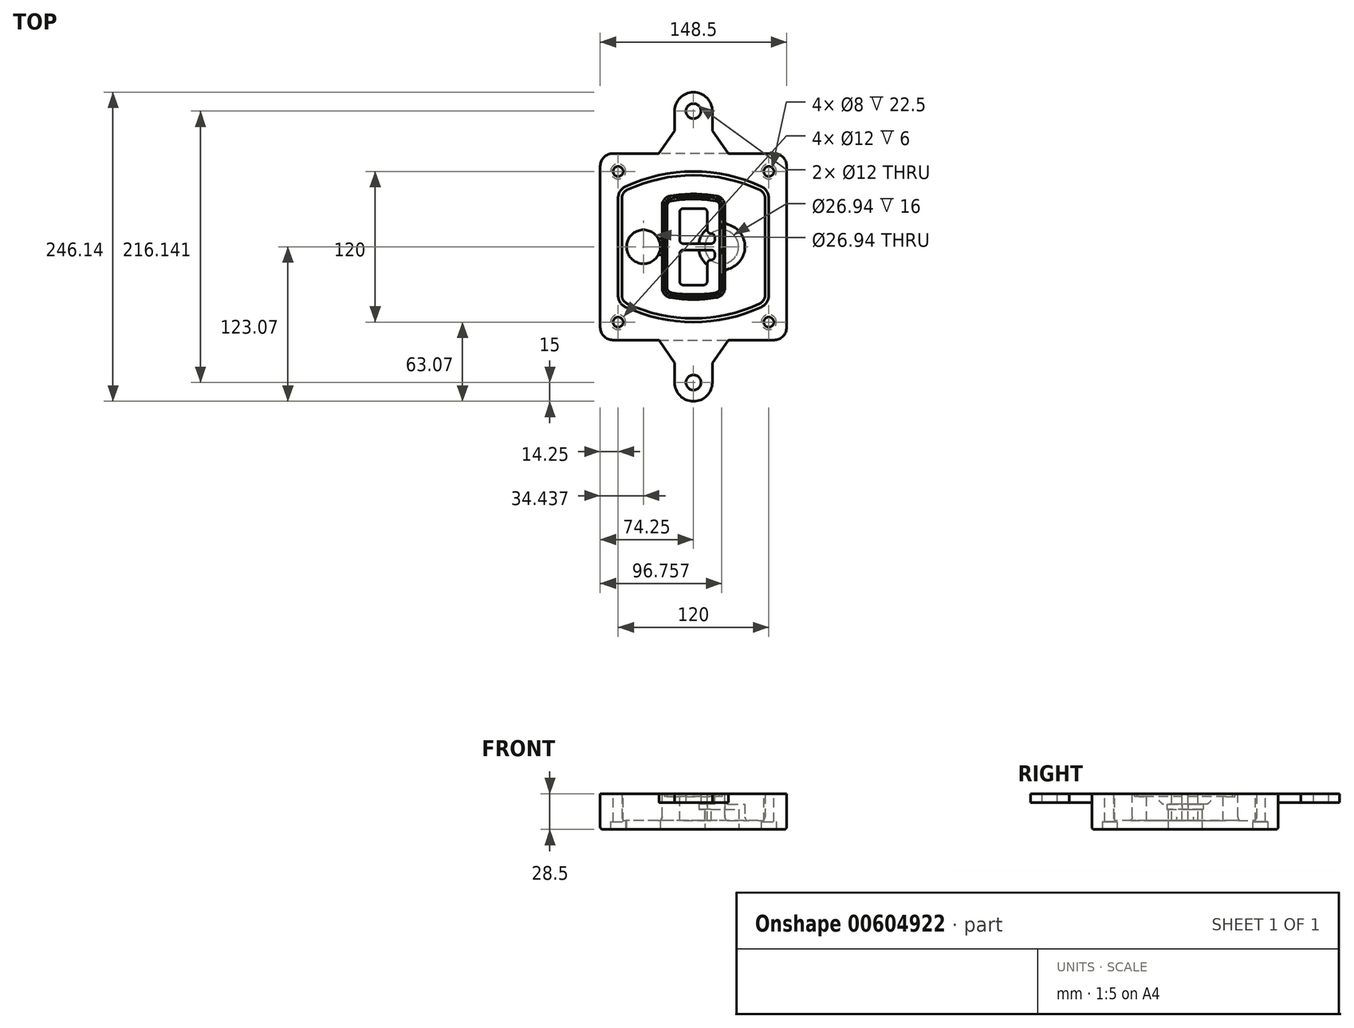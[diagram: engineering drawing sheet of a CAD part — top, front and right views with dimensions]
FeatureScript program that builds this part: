
annotation { "Feature Type Name" : "Feature", "Feature Type Description" : "" }
export const myFeature = defineFeature(function(context is Context, id is Id, definition is map)
    precondition{}
    {
        {
            var Q0;
            Q0=qCreatedBy(makeId("Top.planeOp"),FACE);
            var sketch = newSketch(context, id + "F0", { "sketchPlane" : qUnion([Q0])});
            skPoint(sketch, "E0.rect.middle", {"position": v(0, 0) * mm});
            skLineSegment(sketch, "E1.bottom", {"start": v(-64.25, -74.25) * mm, "end": v(64.25, -74.25) * mm});
            skLineSegment(sketch, "E1.top", {"start": v(-64.25, 74.25) * mm, "end": v(64.25, 74.25) * mm});
            skLineSegment(sketch, "E1.left", {"start": v(-74.25, -64.25) * mm, "end": v(-74.25, 64.25) * mm});
            skLineSegment(sketch, "E1.right", {"start": v(74.25, -64.25) * mm, "end": v(74.25, 64.25) * mm});
            skLineSegment(sketch, "E2", {"start": v(-74.25, 74.25) * mm, "end": v(74.25, -74.25) * mm, "construction": true});
            skLineSegment(sketch, "E3", {"start": v(74.25, 74.25) * mm, "end": v(-74.25, -74.25) * mm, "construction": true});
            skCircle(sketch, "E4", {"center": v(-60, 60) * mm, "radius": 4 * mm});
            skCircle(sketch, "E5", {"center": v(60, 60) * mm, "radius": 4 * mm});
            skCircle(sketch, "E6", {"center": v(60, -60) * mm, "radius": 4 * mm});
            skCircle(sketch, "E7", {"center": v(-60, -60) * mm, "radius": 4 * mm});
            skLineSegment(sketch, "E8", {"start": v(-60, 60) * mm, "end": v(60, 60) * mm, "construction": true});
            skLineSegment(sketch, "E9", {"start": v(60, 60) * mm, "end": v(60, -60) * mm, "construction": true});
            skLineSegment(sketch, "E10", {"start": v(60, -60) * mm, "end": v(-60, -60) * mm, "construction": true});
            skLineSegment(sketch, "E11", {"start": v(-60, -60) * mm, "end": v(-60, 60) * mm, "construction": true});
            skLineSegment(sketch, "E12", {"start": v(-60, 38.83) * mm, "end": v(-60, -38.83) * mm});
            skLineSegment(sketch, "E13", {"start": v(60, 38.83) * mm, "end": v(60, -38.83) * mm});
            skArc(sketch, "E14", {"start": v(54.26, 47.88) * mm, "mid": v(0, 60) * mm, "end": v(-54.26, 47.88) * mm});
            skArc(sketch, "E15", {"start": v(-54.26, -47.88) * mm, "mid": v(0, -60) * mm, "end": v(54.26, -47.88) * mm});
            skLineSegment(sketch, "E16", {"start": v(-60, 0) * mm, "end": v(60, 0) * mm, "construction": true});
            skPoint(sketch, "E17.visualSharp", {"position": v(-60, -45) * mm});
            skArc(sketch, "E17.filletArc", {"start": v(-60, -38.83) * mm, "mid": v(-58.44, -44.2) * mm, "end": v(-54.26, -47.88) * mm});
            skPoint(sketch, "E18.visualSharp", {"position": v(-60, 45) * mm});
            skArc(sketch, "E18.filletArc", {"start": v(-54.26, 47.88) * mm, "mid": v(-58.44, 44.2) * mm, "end": v(-60, 38.83) * mm});
            skPoint(sketch, "E19.visualSharp", {"position": v(60, 45) * mm});
            skArc(sketch, "E19.filletArc", {"start": v(60, 38.83) * mm, "mid": v(58.44, 44.2) * mm, "end": v(54.26, 47.88) * mm});
            skPoint(sketch, "E20.visualSharp", {"position": v(60, -45) * mm});
            skArc(sketch, "E20.filletArc", {"start": v(54.26, -47.88) * mm, "mid": v(58.44, -44.2) * mm, "end": v(60, -38.83) * mm});
            skPoint(sketch, "E21.visualSharp", {"position": v(-74.25, 74.25) * mm});
            skArc(sketch, "E21.filletArc", {"start": v(-64.25, 74.25) * mm, "mid": v(-71.32, 71.32) * mm, "end": v(-74.25, 64.25) * mm});
            skPoint(sketch, "E22.visualSharp", {"position": v(74.25, 74.25) * mm});
            skArc(sketch, "E22.filletArc", {"start": v(74.25, 64.25) * mm, "mid": v(71.32, 71.32) * mm, "end": v(64.25, 74.25) * mm});
            skPoint(sketch, "E23.visualSharp", {"position": v(74.25, -74.25) * mm});
            skArc(sketch, "E23.filletArc", {"start": v(64.25, -74.25) * mm, "mid": v(71.32, -71.32) * mm, "end": v(74.25, -64.25) * mm});
            skPoint(sketch, "E24.visualSharp", {"position": v(-74.25, -74.25) * mm});
            skArc(sketch, "E24.filletArc", {"start": v(-74.25, -64.25) * mm, "mid": v(-71.32, -71.32) * mm, "end": v(-64.25, -74.25) * mm});
            skArc(sketch, "E25.0", {"start": v(57, 38.83) * mm, "mid": v(55.9, 42.58) * mm, "end": v(52.98, 45.17) * mm});
            skLineSegment(sketch, "E25.1", {"start": v(57, 38.83) * mm, "end": v(57, -38.83) * mm});
            skArc(sketch, "E25.2", {"start": v(52.98, -45.17) * mm, "mid": v(55.9, -42.58) * mm, "end": v(57, -38.83) * mm});
            skArc(sketch, "E25.3", {"start": v(-52.98, -45.17) * mm, "mid": v(0, -57) * mm, "end": v(52.98, -45.17) * mm});
            skArc(sketch, "E25.4", {"start": v(-57, -38.83) * mm, "mid": v(-55.9, -42.58) * mm, "end": v(-52.98, -45.17) * mm});
            skArc(sketch, "E25.5", {"start": v(52.98, 45.17) * mm, "mid": v(0, 57) * mm, "end": v(-52.98, 45.17) * mm});
            skLineSegment(sketch, "E25.6", {"start": v(-57, 38.83) * mm, "end": v(-57, -38.83) * mm});
            skArc(sketch, "E25.7", {"start": v(-52.98, 45.17) * mm, "mid": v(-55.9, 42.58) * mm, "end": v(-57, 38.83) * mm});
            skArc(sketch, "E26.0", {"start": v(-55.96, 51.5) * mm, "mid": v(-61.82, 46.33) * mm, "end": v(-64, 38.83) * mm});
            skArc(sketch, "E26.1", {"start": v(55.96, 51.5) * mm, "mid": v(0, 64) * mm, "end": v(-55.96, 51.5) * mm});
            skArc(sketch, "E26.2", {"start": v(64, 38.83) * mm, "mid": v(61.82, 46.33) * mm, "end": v(55.96, 51.5) * mm});
            skLineSegment(sketch, "E26.3", {"start": v(64, 38.83) * mm, "end": v(64, -38.83) * mm});
            skArc(sketch, "E26.4", {"start": v(55.96, -51.5) * mm, "mid": v(61.82, -46.33) * mm, "end": v(64, -38.83) * mm});
            skLineSegment(sketch, "E26.5", {"start": v(-64, 38.83) * mm, "end": v(-64, -38.83) * mm});
            skArc(sketch, "E26.6", {"start": v(-55.96, -51.5) * mm, "mid": v(0, -64) * mm, "end": v(55.96, -51.5) * mm});
            skArc(sketch, "E26.7", {"start": v(-64, -38.83) * mm, "mid": v(-61.82, -46.33) * mm, "end": v(-55.96, -51.5) * mm});
            skSolve(sketch);
        }
        {
            var Q0;
            Q0=makeQuery(id+"F0.imprint","IMPRINT",FACE,{"disambiguationData":[TD([[makeQuery(id+"F0.imprint","IMPRINT",EDGE,{"derivedFrom":sQuery(id+"F0.wireOp",EDGE,"E1.bottom")}),1.0]])]});
            var Q1;
            Q1=makeQuery(id+"F0.imprint","IMPRINT",FACE,{"disambiguationData":[TD([[makeQuery(id+"F0.imprint","IMPRINT",EDGE,{"derivedFrom":sQuery(id+"F0.wireOp",EDGE,"E12")}),1.0]])]});
            var Q2;
            Q2=makeQuery(id+"F0.imprint","IMPRINT",FACE,{"disambiguationData":[TD([[makeQuery(id+"F0.imprint","IMPRINT",EDGE,{"derivedFrom":sQuery(id+"F0.wireOp",EDGE,"E25.0")}),1.0]])]});
            var Q3;
            Q3=makeQuery(id+"F0.imprint","IMPRINT",FACE,{"disambiguationData":[TD([[makeQuery(id+"F0.imprint","IMPRINT",EDGE,{"derivedFrom":sQuery(id+"F0.wireOp",EDGE,"E12")}),-1.0]])]});
            extrude(context, id + "F1", {"entities" : qUnion([Q0, Q1, Q2, Q3]), "oppositeDirection" : true, "depth" : 25 * mm});
        }
        {
            var Q0;
            Q0=makeQuery(id+"F0.imprint","IMPRINT",FACE,{"disambiguationData":[TD([[makeQuery(id+"F0.imprint","IMPRINT",EDGE,{"derivedFrom":sQuery(id+"F0.wireOp",EDGE,"E12")}),1.0]])]});
            extrude(context, id + "F2", {"entities" : qUnion([Q0]), "operationType" : NewBodyOperationType.ADD, "depth" : 3 * mm});
        }
        {
            var Q0;
            Q0=makeQuery(id+"F0.imprint","IMPRINT",FACE,{"disambiguationData":[TD([[makeQuery(id+"F0.imprint","IMPRINT",EDGE,{"derivedFrom":sQuery(id+"F0.wireOp",EDGE,"E25.0")}),1.0]])]});
            extrude(context, id + "F3", {"entities" : qUnion([Q0]), "operationType" : NewBodyOperationType.REMOVE, "oppositeDirection" : true, "depth" : 18 * mm});
        }
        {
            var Q0;
            Q0=makeQuery(id+"F2.opExtrude","CAP_FACE",FACE,{"disambiguationData":[OSD([sQuery(id+"F0.wireOp",EDGE,"E12"),sQuery(id+"F0.wireOp",EDGE,"E13"),sQuery(id+"F0.wireOp",EDGE,"E14"),sQuery(id+"F0.wireOp",EDGE,"E15"),sQuery(id+"F0.wireOp",EDGE,"E17.filletArc"),sQuery(id+"F0.wireOp",EDGE,"E18.filletArc"),sQuery(id+"F0.wireOp",EDGE,"E19.filletArc"),sQuery(id+"F0.wireOp",EDGE,"E20.filletArc"),sQuery(id+"F0.wireOp",EDGE,"E25.0"),sQuery(id+"F0.wireOp",EDGE,"E25.1"),sQuery(id+"F0.wireOp",EDGE,"E25.2"),sQuery(id+"F0.wireOp",EDGE,"E25.3"),sQuery(id+"F0.wireOp",EDGE,"E25.4"),sQuery(id+"F0.wireOp",EDGE,"E25.5"),sQuery(id+"F0.wireOp",EDGE,"E25.6"),sQuery(id+"F0.wireOp",EDGE,"E25.7")])],"isStart":false});
            var sketch = newSketch(context, id + "F4", { "sketchPlane" : qUnion([Q0])});
            skArc(sketch, "E27.0", {"start": v(-18.34, -40.45) * mm, "mid": v(0, -42) * mm, "end": v(18.34, -40.45) * mm});
            skArc(sketch, "E28.0", {"start": v(18.34, 40.45) * mm, "mid": v(0, 42) * mm, "end": v(-18.34, 40.45) * mm});
            skLineSegment(sketch, "E29", {"start": v(-25, 32.57) * mm, "end": v(-25, -32.57) * mm});
            skLineSegment(sketch, "E30", {"start": v(25, 32.57) * mm, "end": v(25, -32.57) * mm});
            skLineSegment(sketch, "E31", {"start": v(-25, 39.1) * mm, "end": v(25, 39.1) * mm, "construction": true});
            skLineSegment(sketch, "E32", {"start": v(-25, -39.1) * mm, "end": v(25, -39.1) * mm, "construction": true});
            skPoint(sketch, "E33.visualSharp", {"position": v(-25, 39.1) * mm});
            skArc(sketch, "E33.filletArc", {"start": v(-18.34, 40.45) * mm, "mid": v(-23.11, 37.73) * mm, "end": v(-25, 32.57) * mm});
            skPoint(sketch, "E34.visualSharp", {"position": v(25, 39.1) * mm});
            skArc(sketch, "E34.filletArc", {"start": v(25, 32.57) * mm, "mid": v(23.11, 37.73) * mm, "end": v(18.34, 40.45) * mm});
            skPoint(sketch, "E35.visualSharp", {"position": v(25, -39.1) * mm});
            skArc(sketch, "E35.filletArc", {"start": v(18.34, -40.45) * mm, "mid": v(23.11, -37.73) * mm, "end": v(25, -32.57) * mm});
            skPoint(sketch, "E36.visualSharp", {"position": v(-25, -39.1) * mm});
            skArc(sketch, "E36.filletArc", {"start": v(-25, -32.57) * mm, "mid": v(-23.11, -37.73) * mm, "end": v(-18.34, -40.45) * mm});
            skArc(sketch, "E37.0", {"start": v(52.98, 45.17) * mm, "mid": v(0, 57) * mm, "end": v(-52.98, 45.17) * mm});
            skArc(sketch, "E37.1", {"start": v(-52.98, 45.17) * mm, "mid": v(-55.9, 42.58) * mm, "end": v(-57, 38.83) * mm});
            skLineSegment(sketch, "E37.2", {"start": v(-57, 38.83) * mm, "end": v(-57, -38.83) * mm});
            skArc(sketch, "E37.3", {"start": v(-57, -38.83) * mm, "mid": v(-55.9, -42.58) * mm, "end": v(-52.98, -45.17) * mm});
            skArc(sketch, "E37.4", {"start": v(-52.98, -45.17) * mm, "mid": v(0, -57) * mm, "end": v(52.98, -45.17) * mm});
            skArc(sketch, "E37.5", {"start": v(52.98, -45.17) * mm, "mid": v(55.9, -42.58) * mm, "end": v(57, -38.83) * mm});
            skLineSegment(sketch, "E37.6", {"start": v(57, 38.83) * mm, "end": v(57, -38.83) * mm});
            skArc(sketch, "E37.7", {"start": v(57, 38.83) * mm, "mid": v(55.9, 42.58) * mm, "end": v(52.98, 45.17) * mm});
            skLineSegment(sketch, "E38.0", {"start": v(23, 32.57) * mm, "end": v(23, -32.57) * mm});
            skArc(sketch, "E38.1", {"start": v(18, -38.48) * mm, "mid": v(21.58, -36.44) * mm, "end": v(23, -32.57) * mm});
            skArc(sketch, "E38.2", {"start": v(-18, -38.48) * mm, "mid": v(0, -40) * mm, "end": v(18, -38.48) * mm});
            skArc(sketch, "E38.3", {"start": v(-23, -32.57) * mm, "mid": v(-21.58, -36.44) * mm, "end": v(-18, -38.48) * mm});
            skLineSegment(sketch, "E38.4", {"start": v(-23, 32.57) * mm, "end": v(-23, -32.57) * mm});
            skArc(sketch, "E38.5", {"start": v(23, 32.57) * mm, "mid": v(21.58, 36.44) * mm, "end": v(18, 38.48) * mm});
            skArc(sketch, "E38.6", {"start": v(-18, 38.48) * mm, "mid": v(-21.58, 36.44) * mm, "end": v(-23, 32.57) * mm});
            skArc(sketch, "E38.7", {"start": v(18, 38.48) * mm, "mid": v(0, 40) * mm, "end": v(-18, 38.48) * mm});
            skArc(sketch, "E39.0", {"start": v(21, 32.57) * mm, "mid": v(20.06, 35.15) * mm, "end": v(17.67, 36.5) * mm});
            skLineSegment(sketch, "E39.1", {"start": v(21, 32.57) * mm, "end": v(21, -32.57) * mm});
            skArc(sketch, "E39.2", {"start": v(17.67, -36.5) * mm, "mid": v(20.06, -35.15) * mm, "end": v(21, -32.57) * mm});
            skArc(sketch, "E39.3", {"start": v(-17.67, -36.5) * mm, "mid": v(0, -38) * mm, "end": v(17.67, -36.5) * mm});
            skArc(sketch, "E39.4", {"start": v(-21, -32.57) * mm, "mid": v(-20.06, -35.15) * mm, "end": v(-17.67, -36.5) * mm});
            skArc(sketch, "E39.5", {"start": v(17.67, 36.5) * mm, "mid": v(0, 38) * mm, "end": v(-17.67, 36.5) * mm});
            skLineSegment(sketch, "E39.6", {"start": v(-21, 32.57) * mm, "end": v(-21, -32.57) * mm});
            skArc(sketch, "E39.7", {"start": v(-17.67, 36.5) * mm, "mid": v(-20.06, 35.15) * mm, "end": v(-21, 32.57) * mm});
            skLineSegment(sketch, "E40", {"start": v(-25, 0) * mm, "end": v(25, 0) * mm, "construction": true});
            skLineSegment(sketch, "E41", {"start": v(-11, 5.5) * mm, "end": v(-11, 27.5) * mm});
            skLineSegment(sketch, "E42", {"start": v(-8, 30.5) * mm, "end": v(8, 30.5) * mm});
            skLineSegment(sketch, "E43", {"start": v(11, 27.5) * mm, "end": v(11, 13.5) * mm});
            skLineSegment(sketch, "E44", {"start": v(14, 10.5) * mm, "end": v(14, 10.5) * mm});
            skLineSegment(sketch, "E45", {"start": v(17, 7.5) * mm, "end": v(17, 5.5) * mm});
            skLineSegment(sketch, "E46", {"start": v(14, 2.5) * mm, "end": v(-8, 2.5) * mm});
            skPoint(sketch, "E47.visualSharp", {"position": v(-11, 30.5) * mm});
            skArc(sketch, "E47.filletArc", {"start": v(-8, 30.5) * mm, "mid": v(-10.12, 29.62) * mm, "end": v(-11, 27.5) * mm});
            skPoint(sketch, "E48.visualSharp", {"position": v(11, 30.5) * mm});
            skArc(sketch, "E48.filletArc", {"start": v(11, 27.5) * mm, "mid": v(10.12, 29.62) * mm, "end": v(8, 30.5) * mm});
            skPoint(sketch, "E49.visualSharp", {"position": v(11, 10.5) * mm});
            skArc(sketch, "E49.filletArc", {"start": v(11, 13.5) * mm, "mid": v(11.88, 11.38) * mm, "end": v(14, 10.5) * mm});
            skPoint(sketch, "E50.visualSharp", {"position": v(17, 10.5) * mm});
            skArc(sketch, "E50.filletArc", {"start": v(17, 7.5) * mm, "mid": v(16.12, 9.62) * mm, "end": v(14, 10.5) * mm});
            skPoint(sketch, "E51.visualSharp", {"position": v(17, 2.5) * mm});
            skArc(sketch, "E51.filletArc", {"start": v(14, 2.5) * mm, "mid": v(16.12, 3.38) * mm, "end": v(17, 5.5) * mm});
            skPoint(sketch, "E52.visualSharp", {"position": v(-11, 2.5) * mm});
            skArc(sketch, "E52.filletArc", {"start": v(-11, 5.5) * mm, "mid": v(-10.12, 3.38) * mm, "end": v(-8, 2.5) * mm});
            skLineSegment(sketch, "E53.0.MirrorCS", {"start": v(14, -2.5) * mm, "end": v(-8, -2.5) * mm});
            skArc(sketch, "E54.0.MirrorCS", {"start": v(-11, -5.5) * mm, "mid": v(-10.12, -3.38) * mm, "end": v(-8, -2.5) * mm});
            skLineSegment(sketch, "E55.0.MirrorCS", {"start": v(-11, -5.5) * mm, "end": v(-11, -27.5) * mm});
            skArc(sketch, "E56.0.MirrorCS", {"start": v(-8, -30.5) * mm, "mid": v(-10.12, -29.62) * mm, "end": v(-11, -27.5) * mm});
            skLineSegment(sketch, "E57.0.MirrorCS", {"start": v(-8, -30.5) * mm, "end": v(8, -30.5) * mm});
            skArc(sketch, "E58.0.MirrorCS", {"start": v(11, -27.5) * mm, "mid": v(10.12, -29.62) * mm, "end": v(8, -30.5) * mm});
            skLineSegment(sketch, "E59.0.MirrorCS", {"start": v(11, -27.5) * mm, "end": v(11, -13.5) * mm});
            skArc(sketch, "E60.0.MirrorCS", {"start": v(11, -13.5) * mm, "mid": v(11.88, -11.38) * mm, "end": v(14, -10.5) * mm});
            skArc(sketch, "E61.0.MirrorCS", {"start": v(17, -7.5) * mm, "mid": v(16.12, -9.62) * mm, "end": v(14, -10.5) * mm});
            skLineSegment(sketch, "E62.0.MirrorCS", {"start": v(17, -7.5) * mm, "end": v(17, -5.5) * mm});
            skArc(sketch, "E63.0.MirrorCS", {"start": v(14, -2.5) * mm, "mid": v(16.12, -3.38) * mm, "end": v(17, -5.5) * mm});
            skSolve(sketch);
        }
        {
            var Q0;
            Q0=makeQuery(id+"F4.imprint","IMPRINT",FACE,{"disambiguationData":[TD([[makeQuery(id+"F4.imprint","IMPRINT",EDGE,{"derivedFrom":sQuery(id+"F4.wireOp",EDGE,"E27.0")}),1.0]])]});
            var Q1;
            Q1=makeQuery(id+"F4.imprint","IMPRINT",FACE,{"disambiguationData":[TD([[makeQuery(id+"F4.imprint","IMPRINT",EDGE,{"derivedFrom":sQuery(id+"F4.wireOp",EDGE,"E38.0")}),-1.0]])]});
            var Q2;
            Q2=makeQuery(id+"F4.imprint","IMPRINT",FACE,{"disambiguationData":[TD([[makeQuery(id+"F4.imprint","IMPRINT",EDGE,{"derivedFrom":sQuery(id+"F4.wireOp",EDGE,"E39.0")}),1.0]])]});
            extrude(context, id + "F5", {"entities" : qUnion([Q0, Q1, Q2]), "operationType" : NewBodyOperationType.ADD, "endBound" : BoundingType.UP_TO_NEXT, "oppositeDirection" : true, "depth" : 25 * mm});
        }
        {
            var Q0;
            Q0=makeQuery(id+"F4.imprint","IMPRINT",FACE,{"disambiguationData":[TD([[makeQuery(id+"F4.imprint","IMPRINT",EDGE,{"derivedFrom":sQuery(id+"F4.wireOp",EDGE,"E38.0")}),-1.0]])]});
            extrude(context, id + "F6", {"entities" : qUnion([Q0]), "operationType" : NewBodyOperationType.REMOVE, "oppositeDirection" : true, "depth" : 2 * mm});
        }
        {
            var Q0;
            Q0=makeQuery(id+"F1.opExtrude","CAP_FACE",FACE,{"disambiguationData":[OSD([sQuery(id+"F0.wireOp",EDGE,"E1.bottom"),sQuery(id+"F0.wireOp",EDGE,"E1.top"),sQuery(id+"F0.wireOp",EDGE,"E1.left"),sQuery(id+"F0.wireOp",EDGE,"E1.right"),sQuery(id+"F0.wireOp",EDGE,"E4"),sQuery(id+"F0.wireOp",EDGE,"E5"),sQuery(id+"F0.wireOp",EDGE,"E6"),sQuery(id+"F0.wireOp",EDGE,"E7"),sQuery(id+"F0.wireOp",EDGE,"E21.filletArc"),sQuery(id+"F0.wireOp",EDGE,"E22.filletArc"),sQuery(id+"F0.wireOp",EDGE,"E23.filletArc"),sQuery(id+"F0.wireOp",EDGE,"E24.filletArc")])],"isStart":false});
            var sketch = newSketch(context, id + "F7", { "sketchPlane" : qUnion([Q0])});
            skCircle(sketch, "E64", {"center": v(22.5, 0) * mm, "radius": 13.47 * mm});
            skCircle(sketch, "E65", {"center": v(-39.81, 0) * mm, "radius": 13.47 * mm});
            skLineSegment(sketch, "E66", {"start": v(74.25, 0) * mm, "end": v(-74.25, 0) * mm});
            skCircle(sketch, "E67", {"center": v(22.5, 0) * mm, "radius": 18.47 * mm});
            skCircle(sketch, "E68", {"center": v(60, -60) * mm, "radius": 6 * mm});
            skCircle(sketch, "E69", {"center": v(-60, -60) * mm, "radius": 6 * mm});
            skCircle(sketch, "E70", {"center": v(-60, 60) * mm, "radius": 6 * mm});
            skCircle(sketch, "E71", {"center": v(60, 60) * mm, "radius": 6 * mm});
            skSolve(sketch);
        }
        {
            var Q0;
            {var subQ1=sQuery(id+"F7.wireOp",EDGE,"E66");var subQ4=sQuery(id+"F7.wireOp",EDGE,"E64");var subQ6=makeQuery(id+"F7.imprint","INTERSECT",VERTEX,{"disambiguationData":[OD(0.0)],"derivedFrom":[subQ4,subQ1]});Q0=makeQuery(id+"F7.imprint","IMPRINT",FACE,{"disambiguationData":[TD([[makeQuery(id+"F7.imprint","IMPRINT",EDGE,{"disambiguationData":[TD([[subQ6,-1.0]])],"derivedFrom":subQ4}),-1.0]])]});}
            var Q1;
            {var subQ0=sQuery(id+"F7.wireOp",EDGE,"E66");var subQ1=sQuery(id+"F7.wireOp",EDGE,"E64");var subQ3=makeQuery(id+"F7.imprint","INTERSECT",VERTEX,{"disambiguationData":[OD(0.0)],"derivedFrom":[subQ1,subQ0]});Q1=makeQuery(id+"F7.imprint","IMPRINT",FACE,{"disambiguationData":[TD([[makeQuery(id+"F7.imprint","IMPRINT",EDGE,{"disambiguationData":[TD([[subQ3,-1.0]])],"derivedFrom":subQ1}),1.0]])]});}
            var Q2;
            {var subQ0=sQuery(id+"F7.wireOp",EDGE,"E66");var subQ1=sQuery(id+"F7.wireOp",EDGE,"E64");var subQ3=makeQuery(id+"F7.imprint","INTERSECT",VERTEX,{"disambiguationData":[OD(0.0)],"derivedFrom":[subQ1,subQ0]});Q2=makeQuery(id+"F7.imprint","IMPRINT",FACE,{"disambiguationData":[TD([[makeQuery(id+"F7.imprint","IMPRINT",EDGE,{"disambiguationData":[TD([[subQ3,1.0]])],"derivedFrom":subQ1}),1.0]])]});}
            var Q3;
            {var subQ1=sQuery(id+"F7.wireOp",EDGE,"E66");var subQ4=sQuery(id+"F7.wireOp",EDGE,"E64");var subQ6=makeQuery(id+"F7.imprint","INTERSECT",VERTEX,{"disambiguationData":[OD(0.0)],"derivedFrom":[subQ4,subQ1]});Q3=makeQuery(id+"F7.imprint","IMPRINT",FACE,{"disambiguationData":[TD([[makeQuery(id+"F7.imprint","IMPRINT",EDGE,{"disambiguationData":[TD([[subQ6,1.0]])],"derivedFrom":subQ4}),-1.0]])]});}
            extrude(context, id + "F8", {"entities" : qUnion([Q0, Q1, Q2, Q3]), "operationType" : NewBodyOperationType.ADD, "oppositeDirection" : true, "depth" : 20 * mm});
        }
        {
            var Q0;
            {var subQ0=sQuery(id+"F7.wireOp",EDGE,"E66");var subQ1=sQuery(id+"F7.wireOp",EDGE,"E64");var subQ3=makeQuery(id+"F7.imprint","INTERSECT",VERTEX,{"disambiguationData":[OD(0.0)],"derivedFrom":[subQ1,subQ0]});Q0=makeQuery(id+"F7.imprint","IMPRINT",FACE,{"disambiguationData":[TD([[makeQuery(id+"F7.imprint","IMPRINT",EDGE,{"disambiguationData":[TD([[subQ3,-1.0]])],"derivedFrom":subQ1}),1.0]])]});}
            var Q1;
            {var subQ0=sQuery(id+"F7.wireOp",EDGE,"E66");var subQ1=sQuery(id+"F7.wireOp",EDGE,"E64");var subQ3=makeQuery(id+"F7.imprint","INTERSECT",VERTEX,{"disambiguationData":[OD(0.0)],"derivedFrom":[subQ1,subQ0]});Q1=makeQuery(id+"F7.imprint","IMPRINT",FACE,{"disambiguationData":[TD([[makeQuery(id+"F7.imprint","IMPRINT",EDGE,{"disambiguationData":[TD([[subQ3,1.0]])],"derivedFrom":subQ1}),1.0]])]});}
            extrude(context, id + "F9", {"entities" : qUnion([Q0, Q1]), "operationType" : NewBodyOperationType.REMOVE, "oppositeDirection" : true, "depth" : 16 * mm});
        }
        {
            var Q0;
            {var subQ0=sQuery(id+"F7.wireOp",EDGE,"E66");var subQ1=sQuery(id+"F7.wireOp",EDGE,"E65");var subQ3=makeQuery(id+"F7.imprint","INTERSECT",VERTEX,{"disambiguationData":[OD(0.0)],"derivedFrom":[subQ1,subQ0]});Q0=makeQuery(id+"F7.imprint","IMPRINT",FACE,{"disambiguationData":[TD([[makeQuery(id+"F7.imprint","IMPRINT",EDGE,{"disambiguationData":[TD([[subQ3,-1.0]])],"derivedFrom":subQ1}),1.0]])]});}
            var Q1;
            {var subQ0=sQuery(id+"F7.wireOp",EDGE,"E66");var subQ1=sQuery(id+"F7.wireOp",EDGE,"E65");var subQ3=makeQuery(id+"F7.imprint","INTERSECT",VERTEX,{"disambiguationData":[OD(0.0)],"derivedFrom":[subQ1,subQ0]});Q1=makeQuery(id+"F7.imprint","IMPRINT",FACE,{"disambiguationData":[TD([[makeQuery(id+"F7.imprint","IMPRINT",EDGE,{"disambiguationData":[TD([[subQ3,1.0]])],"derivedFrom":subQ1}),1.0]])]});}
            extrude(context, id + "F10", {"entities" : qUnion([Q0, Q1]), "operationType" : NewBodyOperationType.REMOVE, "oppositeDirection" : true, "depth" : 25 * mm});
        }
        {
            var Q0;
            Q0=makeQuery(id+"F7.imprint","IMPRINT",FACE,{"disambiguationData":[TD([[makeQuery(id+"F7.imprint","IMPRINT",EDGE,{"derivedFrom":sQuery(id+"F7.wireOp",EDGE,"E68")}),1.0]])]});
            var Q1;
            Q1=makeQuery(id+"F7.imprint","IMPRINT",FACE,{"disambiguationData":[TD([[makeQuery(id+"F7.imprint","IMPRINT",EDGE,{"derivedFrom":makeQuery(id+"F1.opExtrude","CAP_EDGE",EDGE,{"disambiguationData":[OSD([sQuery(id+"F0.wireOp",EDGE,"E5")])],"isStart":false})}),-1.0]])]});
            var Q2;
            Q2=makeQuery(id+"F7.imprint","IMPRINT",FACE,{"disambiguationData":[TD([[makeQuery(id+"F7.imprint","IMPRINT",EDGE,{"derivedFrom":sQuery(id+"F7.wireOp",EDGE,"E69")}),1.0]])]});
            var Q3;
            Q3=makeQuery(id+"F7.imprint","IMPRINT",FACE,{"disambiguationData":[TD([[makeQuery(id+"F7.imprint","IMPRINT",EDGE,{"derivedFrom":makeQuery(id+"F1.opExtrude","CAP_EDGE",EDGE,{"disambiguationData":[OSD([sQuery(id+"F0.wireOp",EDGE,"E4")])],"isStart":false})}),-1.0]])]});
            var Q4;
            Q4=makeQuery(id+"F7.imprint","IMPRINT",FACE,{"disambiguationData":[TD([[makeQuery(id+"F7.imprint","IMPRINT",EDGE,{"derivedFrom":sQuery(id+"F7.wireOp",EDGE,"E70")}),1.0]])]});
            var Q5;
            Q5=makeQuery(id+"F7.imprint","IMPRINT",FACE,{"disambiguationData":[TD([[makeQuery(id+"F7.imprint","IMPRINT",EDGE,{"derivedFrom":makeQuery(id+"F1.opExtrude","CAP_EDGE",EDGE,{"disambiguationData":[OSD([sQuery(id+"F0.wireOp",EDGE,"E7")])],"isStart":false})}),-1.0]])]});
            var Q6;
            Q6=makeQuery(id+"F7.imprint","IMPRINT",FACE,{"disambiguationData":[TD([[makeQuery(id+"F7.imprint","IMPRINT",EDGE,{"derivedFrom":sQuery(id+"F7.wireOp",EDGE,"E71")}),1.0]])]});
            var Q7;
            Q7=makeQuery(id+"F7.imprint","IMPRINT",FACE,{"disambiguationData":[TD([[makeQuery(id+"F7.imprint","IMPRINT",EDGE,{"derivedFrom":makeQuery(id+"F1.opExtrude","CAP_EDGE",EDGE,{"disambiguationData":[OSD([sQuery(id+"F0.wireOp",EDGE,"E6")])],"isStart":false})}),-1.0]])]});
            extrude(context, id + "F11", {"entities" : qUnion([Q0, Q1, Q2, Q3, Q4, Q5, Q6, Q7]), "operationType" : NewBodyOperationType.REMOVE, "oppositeDirection" : true, "depth" : 6 * mm});
        }
        {
            var Q0;
            Q0=makeQuery(id+"F9.boolean.opBoolean","COPY",FACE,{"derivedFrom":makeQuery(id+"F9.opExtrude","CAP_FACE",FACE,{"disambiguationData":[OSD([sQuery(id+"F7.wireOp",EDGE,"E64")])],"isStart":false})});
            var sketch = newSketch(context, id + "F12", { "sketchPlane" : qUnion([Q0])});
            skArc(sketch, "E72.0", {"start": v(11, 14.45) * mm, "mid": v(6.45, 9.13) * mm, "end": v(4.2, 2.5) * mm});
            skArc(sketch, "E72.1", {"start": v(4.2, -2.5) * mm, "mid": v(6.45, -9.13) * mm, "end": v(11, -14.45) * mm});
            skLineSegment(sketch, "E73", {"start": v(4.2, -2.5) * mm, "end": v(14, -2.5) * mm});
            skLineSegment(sketch, "E74.0", {"start": v(14, 2.5) * mm, "end": v(4.2, 2.5) * mm});
            skArc(sketch, "E74.1", {"start": v(14, 2.5) * mm, "mid": v(16.12, 3.38) * mm, "end": v(17, 5.5) * mm});
            skLineSegment(sketch, "E74.2", {"start": v(17, 7.5) * mm, "end": v(17, 5.5) * mm});
            skArc(sketch, "E74.3", {"start": v(17, 7.5) * mm, "mid": v(16.12, 9.62) * mm, "end": v(14, 10.5) * mm});
            skArc(sketch, "E74.4", {"start": v(11, 13.5) * mm, "mid": v(11.88, 11.38) * mm, "end": v(14, 10.5) * mm});
            skLineSegment(sketch, "E74.5", {"start": v(11, 14.45) * mm, "end": v(11, 13.5) * mm});
            skLineSegment(sketch, "E74.7", {"start": v(14, -2.5) * mm, "end": v(4.2, -2.5) * mm});
            skArc(sketch, "E74.8", {"start": v(14, -2.5) * mm, "mid": v(16.12, -3.38) * mm, "end": v(17, -5.5) * mm});
            skLineSegment(sketch, "E74.9", {"start": v(17, -7.5) * mm, "end": v(17, -5.5) * mm});
            skArc(sketch, "E74.10", {"start": v(17, -7.5) * mm, "mid": v(16.12, -9.62) * mm, "end": v(14, -10.5) * mm});
            skArc(sketch, "E74.11", {"start": v(11, -13.5) * mm, "mid": v(11.88, -11.38) * mm, "end": v(14, -10.5) * mm});
            skLineSegment(sketch, "E74.12", {"start": v(11, -14.45) * mm, "end": v(11, -13.5) * mm});
            skPoint(sketch, "E75.orphan", {"position": v(11, -27.5) * mm});
            skPoint(sketch, "E76.orphan", {"position": v(-8, -2.5) * mm});
            skPoint(sketch, "E77.orphan", {"position": v(-8, 2.5) * mm});
            skPoint(sketch, "E78.orphan", {"position": v(11, 27.5) * mm});
            skSolve(sketch);
        }
        {
            var Q0;
            {var subQ7=sQuery(id+"F12.wireOp",EDGE,"E72.0");var subQ14=sQuery(id+"F12.wireOp",EDGE,"E72.1");var subQ16=sQuery(id+"F12.wireOp",EDGE,"E74.1");var subQ18=sQuery(id+"F12.wireOp",EDGE,"E74.8");Q0=qUnion([makeQuery(id+"F12.imprint","IMPRINT",FACE,{"disambiguationData":[TD([[makeQuery(id+"F12.imprint","IMPRINT",EDGE,{"derivedFrom":subQ7}),1.0]])]}),makeQuery(id+"F12.imprint","IMPRINT",FACE,{"disambiguationData":[TD([[makeQuery(id+"F12.imprint","IMPRINT",EDGE,{"derivedFrom":subQ14}),1.0]])]}),makeQuery(id+"F12.imprint","IMPRINT",FACE,{"disambiguationData":[TD([[makeQuery(id+"F12.imprint","IMPRINT",EDGE,{"derivedFrom":subQ16}),1.0]])]}),makeQuery(id+"F12.imprint","IMPRINT",FACE,{"disambiguationData":[TD([[makeQuery(id+"F12.imprint","IMPRINT",EDGE,{"derivedFrom":subQ18}),-1.0]])]})]);}
            var Q1;
            Q1=makeQuery(id+"F5.boolean.opBoolean","SPLIT",FACE,{"disambiguationData":[TD([makeQuery(id+"F5.opExtrude","SWEPT_FACE",FACE,{"disambiguationData":[OSD([sQuery(id+"F4.wireOp",EDGE,"E41")])]})])],"derivedFrom":makeQuery(id+"F3.boolean.opBoolean","COPY",FACE,{"derivedFrom":makeQuery(id+"F3.opExtrude","CAP_FACE",FACE,{"disambiguationData":[OSD([sQuery(id+"F0.wireOp",EDGE,"E25.0"),sQuery(id+"F0.wireOp",EDGE,"E25.1"),sQuery(id+"F0.wireOp",EDGE,"E25.2"),sQuery(id+"F0.wireOp",EDGE,"E25.3"),sQuery(id+"F0.wireOp",EDGE,"E25.4"),sQuery(id+"F0.wireOp",EDGE,"E25.5"),sQuery(id+"F0.wireOp",EDGE,"E25.6"),sQuery(id+"F0.wireOp",EDGE,"E25.7")])],"isStart":false})})});
            extrude(context, id + "F13", {"entities" : qUnion([Q0]), "operationType" : NewBodyOperationType.REMOVE, "endBound" : BoundingType.UP_TO_SURFACE, "endBoundEntityFace" : qUnion([Q1]), "depth" : 25 * mm});
        }
        {
            var Q0;
            Q0=makeQuery(id+"F3.boolean.opBoolean","COPY",EDGE,{"derivedFrom":makeQuery(id+"F3.opExtrude","CAP_EDGE",EDGE,{"disambiguationData":[OSD([sQuery(id+"F0.wireOp",EDGE,"E25.6")])],"isStart":false})});
            var Q1;
            Q1=makeQuery(id+"F8.boolean.opBoolean","INTERSECT",EDGE,{"derivedFrom":[makeQuery(id+"F5.opExtrude","SWEPT_FACE",FACE,{"disambiguationData":[OSD([sQuery(id+"F4.wireOp",EDGE,"E30")])]}),makeQuery(id+"F8.opExtrude","CAP_FACE",FACE,{"disambiguationData":[OSD([sQuery(id+"F7.wireOp",EDGE,"E67")])],"isStart":false})]});
            var Q2;
            Q2=makeQuery(id+"F8.boolean.opBoolean","INTERSECT",EDGE,{"disambiguationData":[OD(1.0)],"derivedFrom":[makeQuery(id+"F5.opExtrude","SWEPT_FACE",FACE,{"disambiguationData":[OSD([sQuery(id+"F4.wireOp",EDGE,"E30")])]}),makeQuery(id+"F8.opExtrude","SWEPT_FACE",FACE,{"disambiguationData":[OSD([sQuery(id+"F7.wireOp",EDGE,"E67")])]})]});
            var Q3;
            {var subQ0=sQuery(id+"F4.wireOp",EDGE,"E30");Q3=makeQuery(id+"F8.boolean.opBoolean","SPLIT",EDGE,{"disambiguationData":[TD([makeQuery(id+"F5.opExtrude","SWEPT_FACE",FACE,{"disambiguationData":[OSD([sQuery(id+"F4.wireOp",EDGE,"E35.filletArc")])]})])],"derivedFrom":makeQuery(id+"F5.opExtrude","CAP_EDGE",EDGE,{"disambiguationData":[OSD([subQ0])],"isStart":false})});}
            var Q4;
            {var subQ0=sQuery(id+"F0.wireOp",EDGE,"E25.7");var subQ1=sQuery(id+"F0.wireOp",EDGE,"E25.1");var subQ2=sQuery(id+"F0.wireOp",EDGE,"E25.6");var subQ3=sQuery(id+"F0.wireOp",EDGE,"E25.5");var subQ4=sQuery(id+"F0.wireOp",EDGE,"E25.4");var subQ5=sQuery(id+"F0.wireOp",EDGE,"E25.0");var subQ6=sQuery(id+"F0.wireOp",EDGE,"E25.2");var subQ7=sQuery(id+"F0.wireOp",EDGE,"E25.3");Q4=makeQuery(id+"F8.boolean.opBoolean","INTERSECT",EDGE,{"derivedFrom":[makeQuery(id+"F5.boolean.opBoolean","SPLIT",FACE,{"disambiguationData":[TD([makeQuery(id+"F2.opExtrude","SWEPT_FACE",FACE,{"disambiguationData":[OSD([subQ5])]})])],"derivedFrom":makeQuery(id+"F3.boolean.opBoolean","COPY",FACE,{"derivedFrom":makeQuery(id+"F3.opExtrude","CAP_FACE",FACE,{"disambiguationData":[OSD([subQ5,subQ1,subQ6,subQ7,subQ4,subQ3,subQ2,subQ0])],"isStart":false})})}),makeQuery(id+"F8.opExtrude","SWEPT_FACE",FACE,{"disambiguationData":[OSD([sQuery(id+"F7.wireOp",EDGE,"E67")])]})]});}
            var Q5;
            Q5=makeQuery(id+"F8.boolean.opBoolean","INTERSECT",EDGE,{"disambiguationData":[OD(0.0)],"derivedFrom":[makeQuery(id+"F5.opExtrude","SWEPT_FACE",FACE,{"disambiguationData":[OSD([sQuery(id+"F4.wireOp",EDGE,"E30")])]}),makeQuery(id+"F8.opExtrude","SWEPT_FACE",FACE,{"disambiguationData":[OSD([sQuery(id+"F7.wireOp",EDGE,"E67")])]})]});
            fillet(context, id + "F14", {"entities" : qUnion([Q0, Q1, Q2, Q3, Q4, Q5]), "radius" : 3 * mm, "tangentPropagation" : true, "allowEdgeOverflow" : false});
        }
        {
            var Q0;
            Q0=makeQuery(id+"F1.opExtrude","CAP_EDGE",EDGE,{"disambiguationData":[OSD([sQuery(id+"F0.wireOp",EDGE,"E1.bottom")])],"isStart":false});
            fillet(context, id + "F15", {"entities" : qUnion([Q0]), "radius" : 2 * mm, "tangentPropagation" : true, "allowEdgeOverflow" : false});
        }
        {
            var Q0;
            {var subQ0=sQuery(id+"F0.wireOp",EDGE,"E21.filletArc");var subQ1=sQuery(id+"F0.wireOp",EDGE,"E7");var subQ2=sQuery(id+"F0.wireOp",EDGE,"E6");var subQ3=sQuery(id+"F0.wireOp",EDGE,"E5");var subQ4=sQuery(id+"F0.wireOp",EDGE,"E4");var subQ5=sQuery(id+"F0.wireOp",EDGE,"E22.filletArc");var subQ6=sQuery(id+"F0.wireOp",EDGE,"E1.bottom");var subQ7=sQuery(id+"F0.wireOp",EDGE,"E1.right");var subQ8=sQuery(id+"F0.wireOp",EDGE,"E1.top");var subQ9=sQuery(id+"F0.wireOp",EDGE,"E1.left");var subQ10=sQuery(id+"F0.wireOp",EDGE,"E23.filletArc");var subQ11=sQuery(id+"F0.wireOp",EDGE,"E24.filletArc");Q0=makeQuery(id+"F2.boolean.opBoolean","SPLIT",FACE,{"disambiguationData":[TD([makeQuery(id+"F1.opExtrude","SWEPT_FACE",FACE,{"disambiguationData":[OSD([subQ6])]})])],"derivedFrom":makeQuery(id+"F1.opExtrude","CAP_FACE",FACE,{"disambiguationData":[OSD([subQ6,subQ8,subQ9,subQ7,subQ4,subQ3,subQ2,subQ1,subQ0,subQ5,subQ10,subQ11])],"isStart":true})});}
            var sketch = newSketch(context, id + "F16", { "sketchPlane" : qUnion([Q0])});
            skSolve(sketch);
        }
        {
            var Q0;
            Q0=makeQuery(id+"F16.imprint","IMPRINT",FACE,{"disambiguationData":[TD([[makeQuery(id+"F16.imprint","IMPRINT",EDGE,{"derivedFrom":makeQuery(id+"F1.opExtrude","CAP_EDGE",EDGE,{"disambiguationData":[OSD([sQuery(id+"F0.wireOp",EDGE,"E1.bottom")])],"isStart":true})}),1.0]])]});
            var sketch = newSketch(context, id + "F17", { "sketchPlane" : qUnion([Q0])});
            skLineSegment(sketch, "E79", {"start": v(74.25, -18) * mm, "end": v(92.25, -13) * mm});
            skLineSegment(sketch, "E80", {"start": v(92.25, -13) * mm, "end": v(104.25, -13) * mm});
            skLineSegment(sketch, "E81", {"start": v(74.25, 18) * mm, "end": v(92.25, 13) * mm});
            skLineSegment(sketch, "E82", {"start": v(92.25, 13) * mm, "end": v(103.83, 13) * mm});
            skLineSegment(sketch, "E83", {"start": v(74.25, 0) * mm, "end": v(104.25, 0) * mm});
            skCircle(sketch, "E84", {"center": v(104.25, 0) * mm, "radius": 6 * mm});
            skArc(sketch, "E85", {"start": v(104.25, -13) * mm, "mid": v(117.25, 0.21) * mm, "end": v(103.83, 13) * mm});
            skLineSegment(sketch, "E86", {"start": v(64.3, 74.33) * mm, "end": v(-63.77, 74.33) * mm, "construction": true});
            skSolve(sketch);
        }
        {
            var Q0;
            Q0=makeQuery(id+"F16.imprint","IMPRINT",FACE,{"disambiguationData":[TD([[makeQuery(id+"F16.imprint","IMPRINT",EDGE,{"derivedFrom":makeQuery(id+"F1.opExtrude","CAP_EDGE",EDGE,{"disambiguationData":[OSD([sQuery(id+"F0.wireOp",EDGE,"E1.bottom")])],"isStart":true})}),1.0]])]});
            var sketch = newSketch(context, id + "F18", { "sketchPlane" : qUnion([Q0])});
            skLineSegment(sketch, "E87", {"start": v(-27.96, 74.09) * mm, "end": v(-15, 92.33) * mm});
            skLineSegment(sketch, "E88", {"start": v(-15, 92.33) * mm, "end": v(-15, 108.07) * mm});
            skLineSegment(sketch, "E89.MirrorCS", {"start": v(15, 92.33) * mm, "end": v(15, 108.07) * mm});
            skLineSegment(sketch, "E90.MirrorCS", {"start": v(27.96, 74.09) * mm, "end": v(15, 92.33) * mm});
            skArc(sketch, "E91", {"start": v(15, 108.07) * mm, "mid": v(0, 123.07) * mm, "end": v(-15, 108.07) * mm});
            skCircle(sketch, "E92", {"center": v(0, 108.07) * mm, "radius": 6 * mm});
            skLineSegment(sketch, "E93", {"start": v(0, 108.07) * mm, "end": v(0, 74.09) * mm});
            skPoint(sketch, "E93.endSnap0", {"position": v(0, 74.09) * mm});
            skLineSegment(sketch, "E94.MirrorCS", {"start": v(-15, -92.33) * mm, "end": v(-15, -108.07) * mm});
            skLineSegment(sketch, "E95.MirrorCS", {"start": v(-27.7, -73.8) * mm, "end": v(-15, -92.33) * mm});
            skArc(sketch, "E96.MirrorCS", {"start": v(15, -108.07) * mm, "mid": v(0, -123.07) * mm, "end": v(-15, -108.07) * mm});
            skCircle(sketch, "E97.MirrorC", {"center": v(0, -108.07) * mm, "radius": 6 * mm});
            skLineSegment(sketch, "E98.MirrorCS", {"start": v(15, -92.33) * mm, "end": v(15, -108.07) * mm});
            skLineSegment(sketch, "E99.MirrorCS", {"start": v(0, -108.07) * mm, "end": v(0, -74.09) * mm});
            skLineSegment(sketch, "E100.MirrorCS", {"start": v(27.96, -74.09) * mm, "end": v(15, -92.33) * mm});
            skPoint(sketch, "E101.MirrorP", {"position": v(0, -74.09) * mm});
            skLineSegment(sketch, "E102", {"start": v(-27.7, -73.8) * mm, "end": v(27.96, -74.09) * mm});
            skLineSegment(sketch, "E103", {"start": v(-27.96, 74.09) * mm, "end": v(27.96, 74.09) * mm});
            skSolve(sketch);
        }
        {
            var Q0;
            {var subQ4=sQuery(id+"F18.wireOp",EDGE,"E88");Q0=makeQuery(id+"F18.imprint","IMPRINT",FACE,{"disambiguationData":[TD([[makeQuery(id+"F18.imprint","IMPRINT",EDGE,{"derivedFrom":subQ4}),-1.0]])]});}
            var Q1;
            {var subQ1=sQuery(id+"F18.wireOp",EDGE,"E94.MirrorCS");Q1=makeQuery(id+"F18.imprint","IMPRINT",FACE,{"disambiguationData":[TD([[makeQuery(id+"F18.imprint","IMPRINT",EDGE,{"derivedFrom":subQ1}),1.0]])]});}
            var Q2;
            Q2=makeQuery(id+"F16.imprint","IMPRINT",FACE,{"disambiguationData":[TD([[makeQuery(id+"F16.imprint","IMPRINT",EDGE,{"derivedFrom":makeQuery(id+"F1.opExtrude","CAP_EDGE",EDGE,{"disambiguationData":[OSD([sQuery(id+"F0.wireOp",EDGE,"E1.bottom")])],"isStart":true})}),1.0]])]});
            extrude(context, id + "F19", {"entities" : qUnion([Q0, Q1, Q2]), "operationType" : NewBodyOperationType.ADD, "endBound" : BoundingType.SYMMETRIC, "depth" : 7 * mm, "offsetDistance" : 25 * mm});
        }
    });
